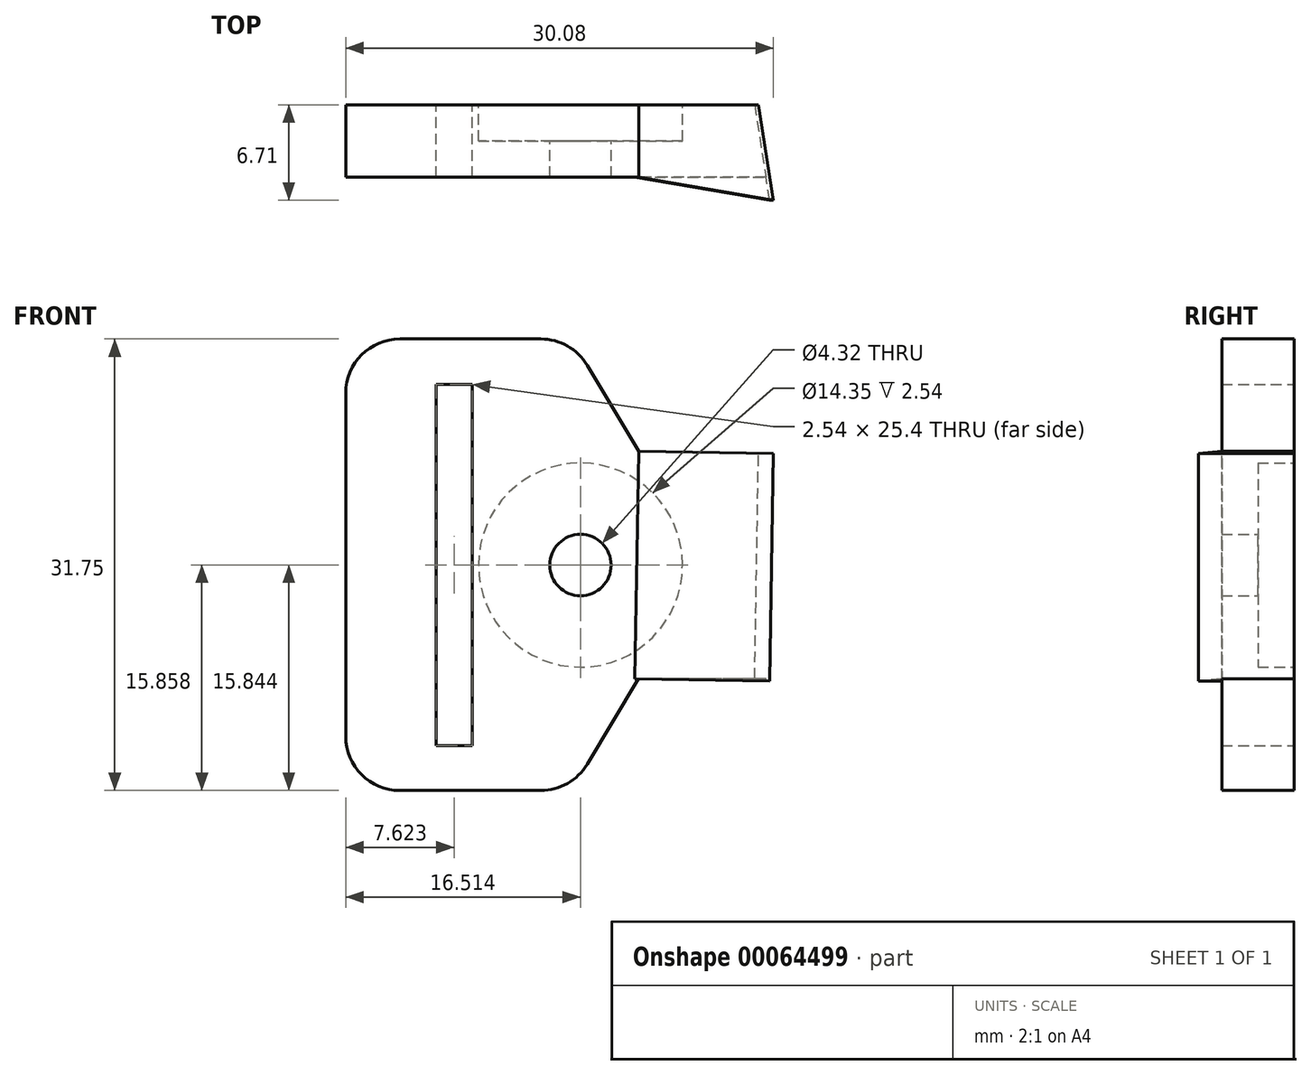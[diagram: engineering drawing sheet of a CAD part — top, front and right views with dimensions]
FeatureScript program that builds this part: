
annotation { "Feature Type Name" : "Feature", "Feature Type Description" : "" }
export const myFeature = defineFeature(function(context is Context, id is Id, definition is map)
    precondition{}
    {
        {
            var Q0;
            Q0=qCreatedBy(makeId("Front.planeOp"),FACE);
            var sketch = newSketch(context, id + "F0", { "sketchPlane" : qUnion([Q0])});
            skLineSegment(sketch, "E0", {"start": v(-27.89, 12.1) * mm, "end": v(-27.89, -12.02) * mm});
            skLineSegment(sketch, "E1", {"start": v(-24.08, -15.83) * mm, "end": v(-14.17, -15.83) * mm});
            skLineSegment(sketch, "E2", {"start": v(-10.9, -13.99) * mm, "end": v(-3.67, -1.96) * mm});
            skLineSegment(sketch, "E3", {"start": v(-3.66, 1.96) * mm, "end": v(-10.9, 14.06) * mm});
            skLineSegment(sketch, "E4", {"start": v(-14.17, 15.92) * mm, "end": v(-24.08, 15.92) * mm});
            skPoint(sketch, "E5.visualSharp", {"position": v(-27.89, 15.92) * mm});
            skArc(sketch, "E5.filletArc", {"start": v(-24.08, 15.92) * mm, "mid": v(-26.77, 14.8) * mm, "end": v(-27.89, 12.1) * mm});
            skPoint(sketch, "E6.visualSharp", {"position": v(-12.01, 15.92) * mm});
            skArc(sketch, "E6.filletArc", {"start": v(-10.9, 14.06) * mm, "mid": v(-12.3, 15.42) * mm, "end": v(-14.17, 15.92) * mm});
            skPoint(sketch, "E7.visualSharp", {"position": v(-27.89, -15.83) * mm});
            skArc(sketch, "E7.filletArc", {"start": v(-27.89, -12.02) * mm, "mid": v(-26.77, -14.72) * mm, "end": v(-24.08, -15.83) * mm});
            skPoint(sketch, "E8.visualSharp", {"position": v(-12.01, -15.83) * mm});
            skArc(sketch, "E8.filletArc", {"start": v(-14.17, -15.83) * mm, "mid": v(-12.3, -15.34) * mm, "end": v(-10.9, -13.99) * mm});
            skPoint(sketch, "E9.visualSharp", {"position": v(-2.49, 0) * mm});
            skArc(sketch, "E9.filletArc", {"start": v(-3.67, -1.96) * mm, "mid": v(-3.12, 0) * mm, "end": v(-3.66, 1.96) * mm});
            skLineSegment(sketch, "E10", {"start": v(-27.89, 0.04) * mm, "end": v(-2.49, 0) * mm});
            skLineSegment(sketch, "E11.bottom", {"start": v(-19, -12.67) * mm, "end": v(-21.54, -12.67) * mm});
            skLineSegment(sketch, "E11.top", {"start": v(-19, 12.73) * mm, "end": v(-21.54, 12.73) * mm});
            skLineSegment(sketch, "E11.left", {"start": v(-19, -12.67) * mm, "end": v(-19, 12.73) * mm});
            skLineSegment(sketch, "E11.right", {"start": v(-21.54, -12.67) * mm, "end": v(-21.54, 12.73) * mm});
            skPoint(sketch, "E11.middle", {"position": v(-20.27, 0.03) * mm});
            skPoint(sketch, "E12.middle", {"position": v(-11.8, 0.01) * mm});
            skCircle(sketch, "E13", {"center": v(-11.38, 0.01) * mm, "radius": 2.16 * mm});
            skLineSegment(sketch, "E14", {"start": v(-7.28, 8.01) * mm, "end": v(2.2, 7.85) * mm});
            skLineSegment(sketch, "E15", {"start": v(2.2, 7.85) * mm, "end": v(1.92, -7.97) * mm});
            skPoint(sketch, "E15.endSnap0", {"position": v(-7.28, -7.97) * mm});
            skLineSegment(sketch, "E16", {"start": v(1.92, -7.97) * mm, "end": v(-7.28, -7.97) * mm});
            skSolve(sketch);
        }
        {
            var Q0;
            {var subQ1=sQuery(id+"F0.wireOp",EDGE,"E3");Q0=makeQuery(id+"F0.imprint","IMPRINT",FACE,{"disambiguationData":[TD([[makeQuery(id+"F0.imprint","IMPRINT",EDGE,{"derivedFrom":subQ1}),1.0]])]});}
            var Q1;
            Q1=makeQuery(id+"F0.imprint","IMPRINT",FACE,{"disambiguationData":[TD([[makeQuery(id+"F0.imprint","IMPRINT",EDGE,{"derivedFrom":sQuery(id+"F0.wireOp",EDGE,"E1")}),1.0]])]});
            var Q2;
            {var subQ6=sQuery(id+"F0.wireOp",EDGE,"E14");Q2=makeQuery(id+"F0.imprint","IMPRINT",FACE,{"disambiguationData":[TD([[makeQuery(id+"F0.imprint","IMPRINT",EDGE,{"derivedFrom":subQ6}),-1.0]])]});}
            extrude(context, id + "F1", {"entities" : qUnion([Q0, Q1, Q2]), "depth" : 5.08 * mm});
        }
        {
            var Q0;
            Q0=makeQuery(id+"F1.opExtrude","CAP_FACE",FACE,{"disambiguationData":[OSD([sQuery(id+"F0.wireOp",EDGE,"E0"),sQuery(id+"F0.wireOp",EDGE,"E1"),sQuery(id+"F0.wireOp",EDGE,"E2"),sQuery(id+"F0.wireOp",EDGE,"E3"),sQuery(id+"F0.wireOp",EDGE,"E4"),sQuery(id+"F0.wireOp",EDGE,"E5.filletArc"),sQuery(id+"F0.wireOp",EDGE,"E6.filletArc"),sQuery(id+"F0.wireOp",EDGE,"E7.filletArc"),sQuery(id+"F0.wireOp",EDGE,"E8.filletArc"),sQuery(id+"F0.wireOp",EDGE,"E9.filletArc"),sQuery(id+"F0.wireOp",EDGE,"E11.bottom"),sQuery(id+"F0.wireOp",EDGE,"E11.top"),sQuery(id+"F0.wireOp",EDGE,"E11.left"),sQuery(id+"F0.wireOp",EDGE,"E11.right"),sQuery(id+"F0.wireOp",EDGE,"E12.bottom"),sQuery(id+"F0.wireOp",EDGE,"E12.top"),sQuery(id+"F0.wireOp",EDGE,"E12.left"),sQuery(id+"F0.wireOp",EDGE,"E12.right"),sQuery(id+"F0.wireOp",EDGE,"E13")])],"isStart":true});
            var sketch = newSketch(context, id + "F2", { "sketchPlane" : qUnion([Q0])});
            skCircle(sketch, "E17", {"center": v(11.38, 0.01) * mm, "radius": 7.18 * mm});
            skSolve(sketch);
        }
        {
            var Q0;
            Q0=makeQuery(id+"F2.imprint","IMPRINT",FACE,{"disambiguationData":[TD([[makeQuery(id+"F2.imprint","IMPRINT",EDGE,{"derivedFrom":sQuery(id+"F2.wireOp",EDGE,"E17")}),1.0]])]});
            extrude(context, id + "F3", {"entities" : qUnion([Q0]), "operationType" : NewBodyOperationType.REMOVE, "oppositeDirection" : true, "depth" : 2.54 * mm});
        }
        {
            var Q0;
            Q0=makeQuery(id+"F1.opExtrude","SWEPT_FACE",FACE,{"disambiguationData":[OSD([sQuery(id+"F0.wireOp",EDGE,"E14")])]});
            var sketch = newSketch(context, id + "F4", { "sketchPlane" : qUnion([Q0])});
            skLineSegment(sketch, "E18", {"start": v(-7.42, -5.08) * mm, "end": v(2.06, -6.71) * mm});
            skLineSegment(sketch, "E19", {"start": v(2.06, -6.71) * mm, "end": v(1.01, 0) * mm});
            skSolve(sketch);
        }
        {
            var Q0;
            {var subQ0=sQuery(id+"F4.wireOp",EDGE,"E18");Q0=makeQuery(id+"F4.imprint","IMPRINT",FACE,{"disambiguationData":[TD([[makeQuery(id+"F4.imprint","IMPRINT",EDGE,{"derivedFrom":subQ0}),1.0]])]});}
            extrude(context, id + "F5", {"entities" : qUnion([Q0]), "operationType" : NewBodyOperationType.ADD, "oppositeDirection" : true, "depth" : 16 * mm});
        }
        {
            var Q0;
            {var subQ1=sQuery(id+"F0.wireOp",EDGE,"E14");var subQ6=makeQuery(id+"F1.opExtrude","SWEPT_EDGE",EDGE,{"disambiguationData":[OSD([subQ1,sQuery(id+"F0.wireOp",EDGE,"E15")])]});Q0=makeQuery(id+"F4.imprint","IMPRINT",FACE,{"disambiguationData":[TD([[makeQuery(id+"F4.imprint","IMPRINT",EDGE,{"derivedFrom":subQ6}),1.0]])]});}
            extrude(context, id + "F6", {"entities" : qUnion([Q0]), "operationType" : NewBodyOperationType.REMOVE, "oppositeDirection" : true, "depth" : 25.4 * mm});
        }
    });
